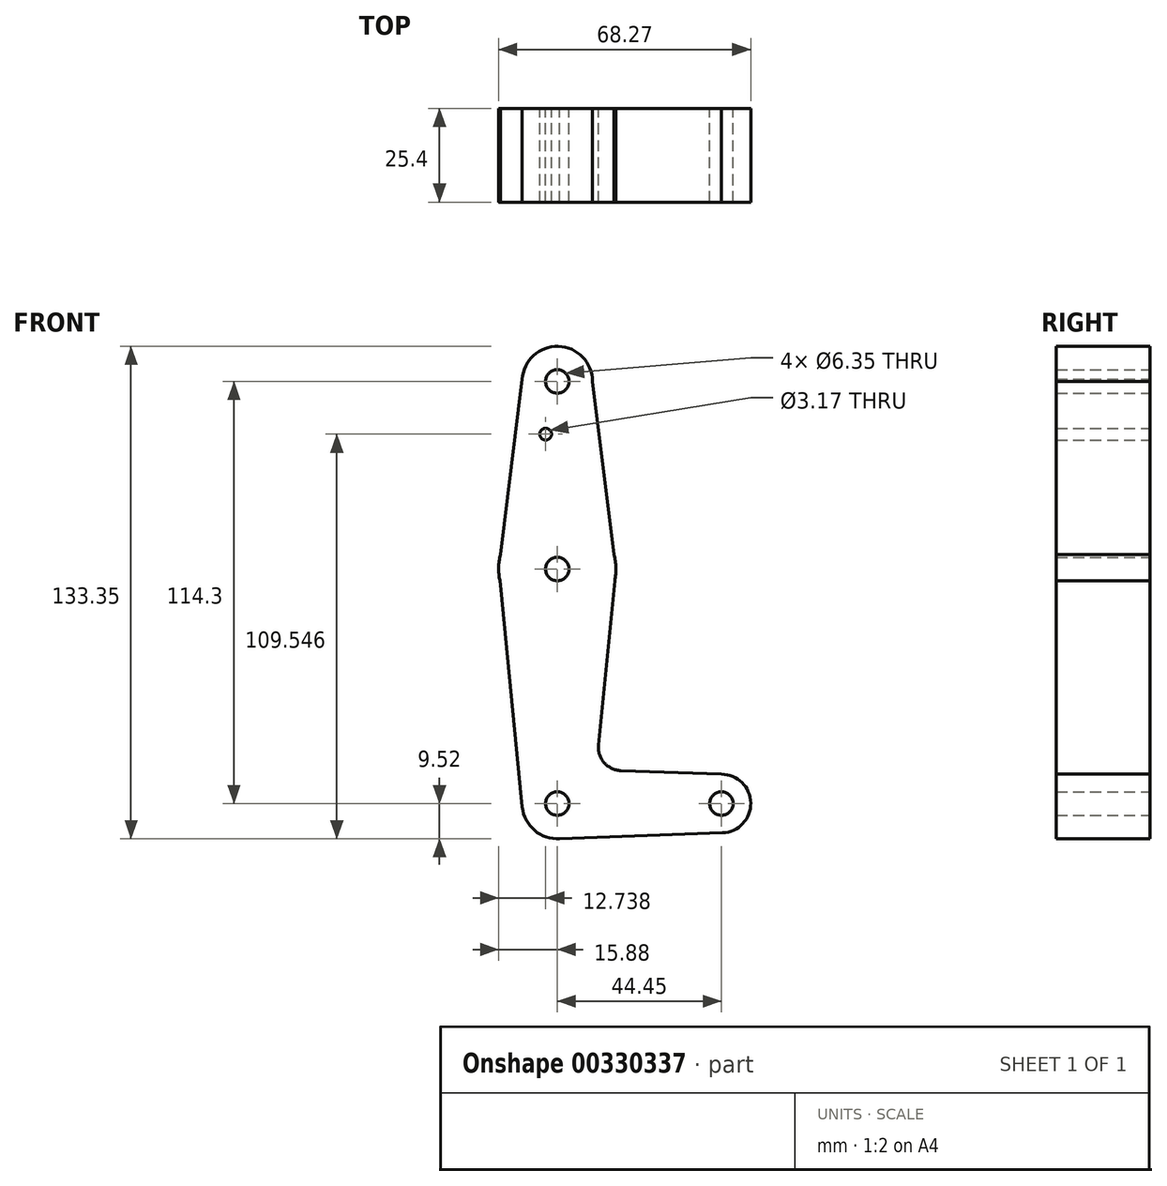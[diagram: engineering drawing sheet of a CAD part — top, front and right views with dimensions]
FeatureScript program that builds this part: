
annotation { "Feature Type Name" : "Feature", "Feature Type Description" : "" }
export const myFeature = defineFeature(function(context is Context, id is Id, definition is map)
    precondition{}
    {
        {
            var Q0;
            Q0=qCreatedBy(makeId("Front.planeOp"),FACE);
            var sketch = newSketch(context, id + "F0", { "sketchPlane" : qUnion([Q0])});
            skLineSegment(sketch, "E0", {"start": v(0, 0) * mm, "end": v(0, -56.85) * mm, "construction": true});
            skLineSegment(sketch, "E1", {"start": v(0, -56.85) * mm, "end": v(44.45, -56.85) * mm, "construction": true});
            skLineSegment(sketch, "E2", {"start": v(0, 0) * mm, "end": v(0, 57.45) * mm, "construction": true});
            skCircle(sketch, "E3", {"center": v(0, 57.45) * mm, "radius": 9.53 * mm});
            skCircle(sketch, "E4", {"center": v(0, 6.65) * mm, "radius": 15.88 * mm});
            skCircle(sketch, "E5", {"center": v(0, -56.85) * mm, "radius": 9.53 * mm});
            skCircle(sketch, "E6", {"center": v(44.45, -56.85) * mm, "radius": 7.94 * mm});
            skLineSegment(sketch, "E7", {"start": v(-9.5, 58.02) * mm, "end": v(-15.87, 6.65) * mm});
            skLineSegment(sketch, "E8", {"start": v(-15.87, 6.65) * mm, "end": v(-9.48, -57.8) * mm});
            skLineSegment(sketch, "E9", {"start": v(9.52, 57.45) * mm, "end": v(15.88, 6.65) * mm});
            skLineSegment(sketch, "E10", {"start": v(15.88, 6.65) * mm, "end": v(11.15, -40.96) * mm});
            skLineSegment(sketch, "E11", {"start": v(44.45, -48.91) * mm, "end": v(17.24, -47.94) * mm});
            skLineSegment(sketch, "E12", {"start": v(0, -66.37) * mm, "end": v(44.73, -64.78) * mm});
            skCircle(sketch, "E13", {"center": v(0, 57.45) * mm, "radius": 3.18 * mm});
            skCircle(sketch, "E14", {"center": v(0, 6.65) * mm, "radius": 3.18 * mm});
            skCircle(sketch, "E15", {"center": v(-3.14, 43.18) * mm, "radius": 1.59 * mm});
            skCircle(sketch, "E16", {"center": v(0, -56.85) * mm, "radius": 3.18 * mm});
            skCircle(sketch, "E17", {"center": v(44.45, -56.85) * mm, "radius": 3.18 * mm});
            skPoint(sketch, "E18.newPointA", {"position": v(0, -47.32) * mm});
            skArc(sketch, "E18.filletArc", {"start": v(11.15, -40.96) * mm, "mid": v(12.69, -45.77) * mm, "end": v(17.24, -47.94) * mm});
            skSolve(sketch);
        }
        {
            var Q0;
            Q0 = qSketchRegion(id + "F0", true);
            extrude(context, id + "F1", {"entities" : qUnion([Q0]), "depth" : 25.4 * mm});
        }
    });
